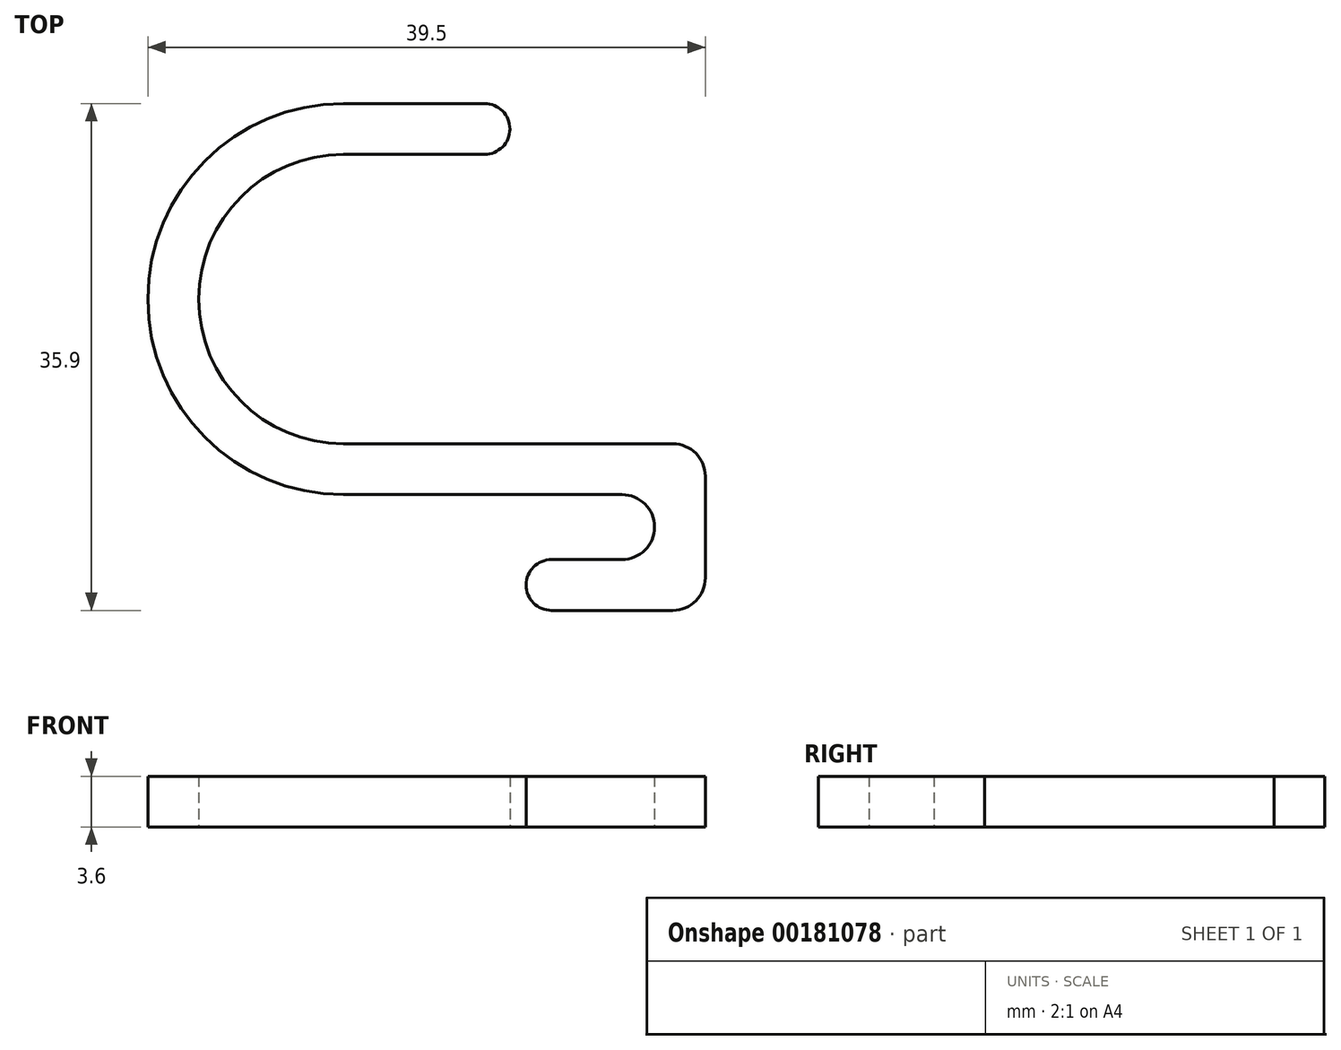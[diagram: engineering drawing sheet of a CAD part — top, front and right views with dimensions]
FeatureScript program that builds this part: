
annotation { "Feature Type Name" : "Feature", "Feature Type Description" : "" }
export const myFeature = defineFeature(function(context is Context, id is Id, definition is map)
    precondition{}
    {
        {
            assignVariable(context, id + "F0", {"name" : "wall", "anyValue" : 3.6});
        }
        {
            var Q0;
            Q0=qCreatedBy(makeId("Top.planeOp"),FACE);
            var sketch = newSketch(context, id + "F1", { "sketchPlane" : qUnion([Q0])});
            skLineSegment(sketch, "E0", {"start": v(-37.6, 0) * mm, "end": v(78.58, 0) * mm, "construction": true});
            skLineSegment(sketch, "E1", {"start": v(0, 37.2) * mm, "end": v(0, -47.53) * mm, "construction": true});
            skLineSegment(sketch, "E2.top", {"start": v(-30, -10.25) * mm, "end": v(3.6, -10.25) * mm, "construction": true});
            skLineSegment(sketch, "E2.left", {"start": v(-30, 10.25) * mm, "end": v(-30, -10.25) * mm, "construction": true});
            skPoint(sketch, "E2.middle", {"position": v(0, 0) * mm});
            skArc(sketch, "E3", {"start": v(-19.75, 10.25) * mm, "mid": v(-30, 0) * mm, "end": v(-19.75, -10.25) * mm});
            skArc(sketch, "E4.0", {"start": v(-19.75, 13.85) * mm, "mid": v(-33.6, 0) * mm, "end": v(-19.75, -13.85) * mm});
            skLineSegment(sketch, "E5", {"start": v(-19.75, 13.85) * mm, "end": v(-9.75, 13.85) * mm});
            skArc(sketch, "E6", {"start": v(-9.75, 10.25) * mm, "mid": v(-7.95, 12.05) * mm, "end": v(-9.75, 13.85) * mm});
            skLineSegment(sketch, "E7", {"start": v(-19.75, -13.85) * mm, "end": v(0, -13.85) * mm});
            skLineSegment(sketch, "E8", {"start": v(0, -13.85) * mm, "end": v(0, -18.45) * mm, "construction": true});
            skLineSegment(sketch, "E9", {"start": v(0, -18.45) * mm, "end": v(-5, -18.45) * mm});
            skLineSegment(sketch, "E10", {"start": v(-5, -18.45) * mm, "end": v(-5, -22.05) * mm, "construction": true});
            skLineSegment(sketch, "E11", {"start": v(-5, -22.05) * mm, "end": v(3.6, -22.05) * mm});
            skLineSegment(sketch, "E12", {"start": v(5.9, -19.75) * mm, "end": v(5.9, -12.55) * mm});
            skArc(sketch, "E13", {"start": v(0, -18.45) * mm, "mid": v(2.3, -16.15) * mm, "end": v(0, -13.85) * mm});
            skArc(sketch, "E14", {"start": v(-5, -18.45) * mm, "mid": v(-6.8, -20.25) * mm, "end": v(-5, -22.05) * mm});
            skPoint(sketch, "E15.visualSharp", {"position": v(5.9, -22.05) * mm});
            skArc(sketch, "E15.filletArc", {"start": v(3.6, -22.05) * mm, "mid": v(5.23, -21.38) * mm, "end": v(5.9, -19.75) * mm});
            skPoint(sketch, "E16.newPointA", {"position": v(30, -10.25) * mm});
            skArc(sketch, "E16.filletArc", {"start": v(5.9, -12.55) * mm, "mid": v(5.23, -10.92) * mm, "end": v(3.6, -10.25) * mm});
            skLineSegment(sketch, "E17", {"start": v(-19.75, -10.25) * mm, "end": v(3.6, -10.25) * mm});
            skLineSegment(sketch, "E18", {"start": v(-19.75, 10.25) * mm, "end": v(-9.75, 10.25) * mm});
            skSolve(sketch);
        }
        {
            var Q0;
            Q0 = qSketchRegion(id + "F1", true);
            extrude(context, id + "F2", {"entities" : qUnion([Q0]), "depth" : (getVariable(context, 'wall')) * mm, "symmetric" : true});
        }
    });
